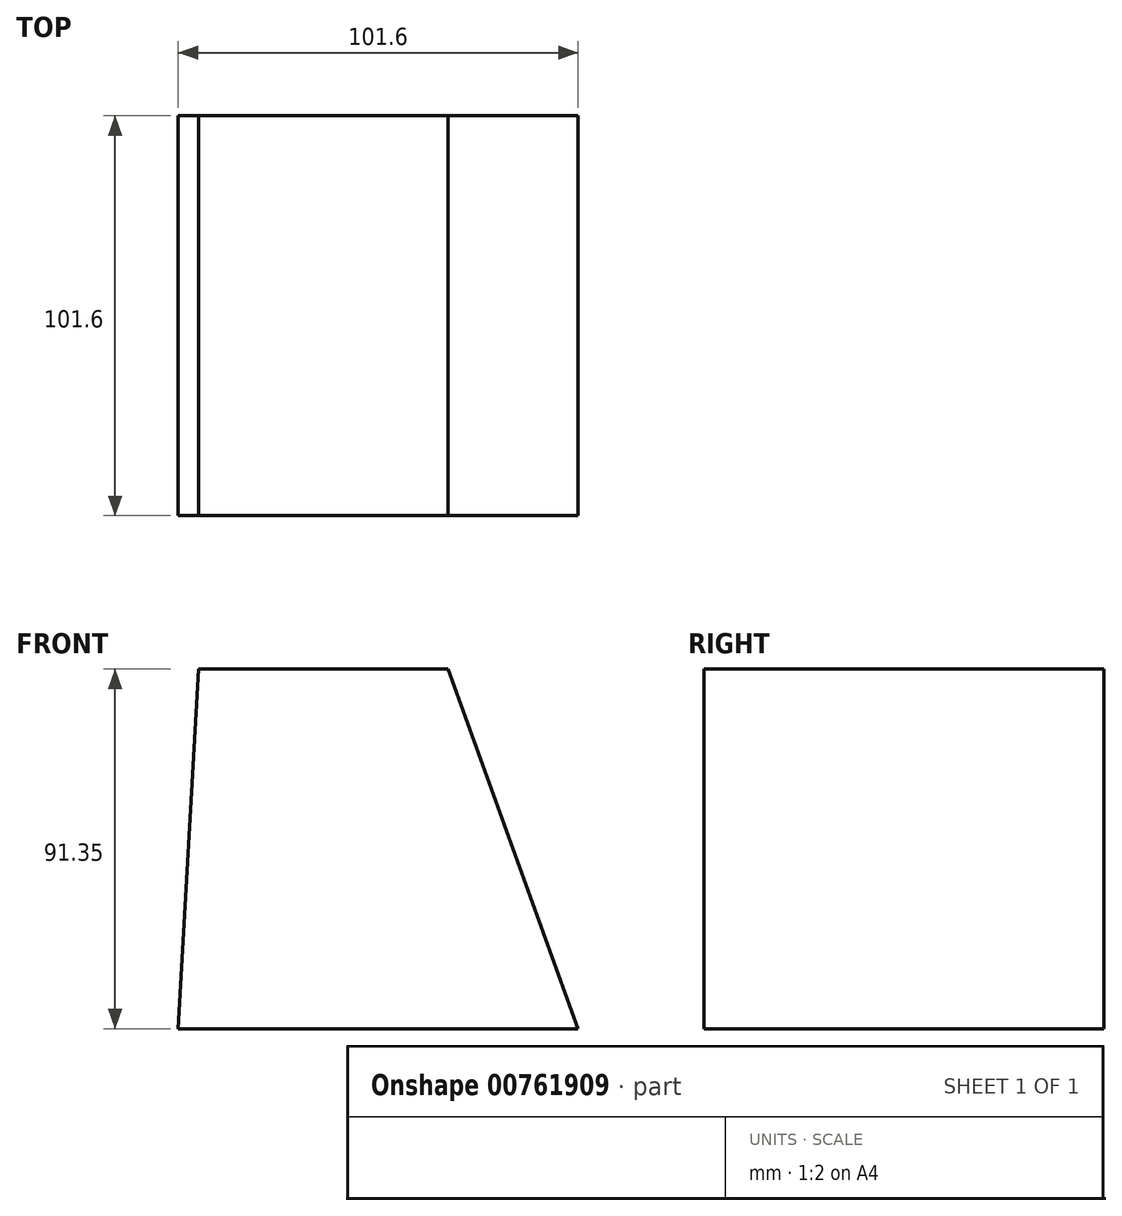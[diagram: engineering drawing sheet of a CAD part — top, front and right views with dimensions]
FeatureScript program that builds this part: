
annotation { "Feature Type Name" : "Feature", "Feature Type Description" : "" }
export const myFeature = defineFeature(function(context is Context, id is Id, definition is map)
    precondition{}
    {
        {
            var Q0;
            Q0=qCreatedBy(makeId("Front.planeOp"),FACE);
            var sketch = newSketch(context, id + "F0", { "sketchPlane" : qUnion([Q0])});
            skLineSegment(sketch, "E0", {"start": v(0, 0) * mm, "end": v(5.19, 91.35) * mm});
            skLineSegment(sketch, "E1", {"start": v(5.19, 91.35) * mm, "end": v(68.55, 91.35) * mm});
            skLineSegment(sketch, "E2", {"start": v(68.55, 87.1) * mm, "end": v(68.55, 91.35) * mm});
            skLineSegment(sketch, "E3", {"start": v(68.55, 91.35) * mm, "end": v(101.6, 0) * mm});
            skLineSegment(sketch, "E4", {"start": v(0, 0) * mm, "end": v(101.6, 0) * mm});
            skSolve(sketch);
        }
        {
            var Q0;
            Q0=makeQuery(id+"F0.imprint","IMPRINT",FACE,{"disambiguationData":[TD([[makeQuery(id+"F0.imprint","IMPRINT",EDGE,{"derivedFrom":sQuery(id+"F0.wireOp",EDGE,"E0")}),-1.0]])]});
            extrude(context, id + "F1", {"entities" : qUnion([Q0]), "depth" : 101.6 * mm, "offsetDistance" : 25.4 * mm});
        }
    });
